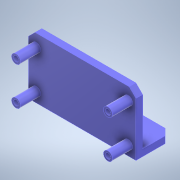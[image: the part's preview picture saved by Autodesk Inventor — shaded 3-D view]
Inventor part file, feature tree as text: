
AUTODESK INVENTOR PART (.ipt)
format: ipt  version: 2022.6 (Build 266554000, 554)  size: 276,992 bytes
history: native  units: mm
features: projected_geometry x9, extrude x7, sketch x5, chamfer x4, hole x2, rib x1, other x1
ambient origin geometry x8: Origin, YZ Plane, XZ Plane, XY Plane, X Axis, Y Axis, Z Axis, Center Point
bodies: Solid1 (feature_tree)
feature tree (29):
  extrude  "Extrusion1"  Depth=44.0mm
  extrude  "Extrusion2"  Depth=3.0mm TaperAngle=0.0deg
  hole  "Hole1"  [1 undecoded]
  rib  "Rib1"
  chamfer  "Chamfer1"  Distance=23.7mm
  hole  "Hole2"  [1 undecoded]
  chamfer  "Chamfer2"  Distance=30.0mm
  extrude  "Extrusion3"  Depth=3.0mm TaperAngle=45.0deg
  extrude  "Extrusion4"  Depth=2.0mm
  other  "Bend Part1"
  extrude  "Extrusion6"  Depth=2.0mm
  chamfer  "Chamfer3"  Distance=4.0mm
  extrude  "Extrusion7"  Depth=2.0mm
  extrude  "Extrusion8"  Depth=9.0mm TaperAngle=0.0deg
  chamfer  "Chamfer4"  Distance=32.0mm
  sketch  "Sketch7"  dims[d0=20.0mm d1=44.0mm]
  projected_geometry  "Projected Loop1"
  sketch  "Sketch9"  dims[d2=2.0mm d3=3.0mm d4=0.0mm]
  projected_geometry  "Projected Loop2"
  sketch  "Sketch10"  dims[d5=16.0mm d6=3.0mm d7=0.0mm]
  projected_geometry  "Projected Loop3"
  projected_geometry  "Projected Loop4"
  projected_geometry  "Projected Loop5"
  sketch  "Sketch11"  dims[d14=2.4mm d15=6.0mm d16=4.0mm d17=2.0mm d18=90.0deg d19=6.0mm d20=0.0mm]
  projected_geometry  "Projected Loop6"
  sketch  "Sketch12"  dims[d21=12.0mm d22=23.7mm d23=1.0mm d24=3.0mm d25=0.0mm d26=0.0mm d27=1.0mm d28=1.0mm d29=2.0mm d30=2.0mm d31=45.0deg d32=30.0mm d33=3.4mm d34=6.0mm d35=4.0mm d36=2.0mm d37=90.0deg d38=6.0mm d39=0.0mm d40=3.0mm d41=2.0mm d42=45.0deg d46=4.0mm d47=4.0mm d49=4.0mm d50=4.0mm d51=9.0mm d52=0.0mm d53=32.0mm d54=20.0mm d55=8.5mm d57=24.0mm d58=3.0mm d59=0.0mm d63=1.0mm d64=1.745329mm d66=1.0mm d67=30.0mm d68=0.0mm d69=0.0mm d70=1.0mm d71=2.0mm d72=45.0deg d73=41.0mm d74=17.0mm d77=10.0mm d78=3.0mm d79=0.0mm d80=0.0mm d81=4.0mm d82=4.0mm d83=2.0mm d84=0.0mm d85=2.0mm d86=2.0mm d87=45.0deg]
  projected_geometry  "Projected Loop7"
  projected_geometry  "Project Cut Edges1"
  projected_geometry  "Project Cut Edges2"
note: 2 required parameter values undecoded (feature->parameter linkage not recoverable at this tier; creation-order binding heuristic only, values carry confidence <= 0.55)
